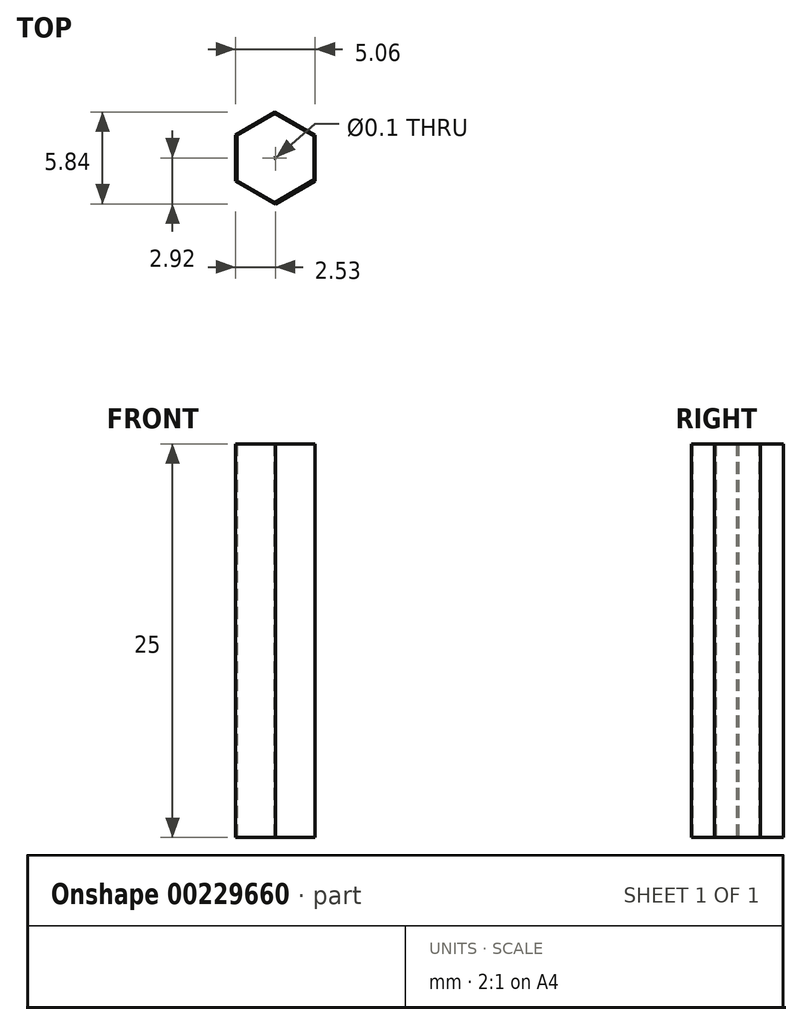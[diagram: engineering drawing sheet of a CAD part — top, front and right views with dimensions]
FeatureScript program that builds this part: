
annotation { "Feature Type Name" : "Feature", "Feature Type Description" : "" }
export const myFeature = defineFeature(function(context is Context, id is Id, definition is map)
    precondition{}
    {
        {
            var Q0;
            Q0=qCreatedBy(makeId("Top.planeOp"),FACE);
            var sketch = newSketch(context, id + "F0", { "sketchPlane" : qUnion([Q0])});
            skLineSegment(sketch, "E0.0", {"start": v(2.53, 1.46) * mm, "end": v(2.53, -1.46) * mm});
            skLineSegment(sketch, "E0.1", {"start": v(2.53, -1.46) * mm, "end": v(0, -2.92) * mm});
            skLineSegment(sketch, "E0.2", {"start": v(0, -2.92) * mm, "end": v(-2.53, -1.46) * mm});
            skLineSegment(sketch, "E0.3", {"start": v(-2.53, -1.46) * mm, "end": v(-2.53, 1.46) * mm});
            skLineSegment(sketch, "E0.4", {"start": v(-2.53, 1.46) * mm, "end": v(0, 2.92) * mm});
            skLineSegment(sketch, "E0.5", {"start": v(0, 2.92) * mm, "end": v(2.53, 1.46) * mm});
            skSolve(sketch);
        }
        {
            var Q0;
            Q0=makeQuery(id+"F0.imprint","IMPRINT",FACE,{"disambiguationData":[TD([[makeQuery(id+"F0.imprint","IMPRINT",EDGE,{"derivedFrom":sQuery(id+"F0.wireOp",EDGE,"E0.0")}),-1.0]])]});
            extrude(context, id + "F1", {"entities" : qUnion([Q0]), "depth" : 25 * mm});
        }
        {
            var Q0;
            Q0=qCreatedBy(makeId("Top.planeOp"),FACE);
            var sketch = newSketch(context, id + "F2", { "sketchPlane" : qUnion([Q0])});
            skLineSegment(sketch, "E1.0", {"start": v(2.5, 1.45) * mm, "end": v(2.5, -1.45) * mm});
            skLineSegment(sketch, "E1.1", {"start": v(2.5, -1.45) * mm, "end": v(0, -2.9) * mm});
            skLineSegment(sketch, "E1.2", {"start": v(0, -2.9) * mm, "end": v(-2.5, -1.45) * mm});
            skLineSegment(sketch, "E1.3", {"start": v(-2.5, -1.45) * mm, "end": v(-2.5, 1.45) * mm});
            skLineSegment(sketch, "E1.4", {"start": v(-2.5, 1.45) * mm, "end": v(0, 2.9) * mm});
            skLineSegment(sketch, "E1.5", {"start": v(0, 2.9) * mm, "end": v(2.5, 1.45) * mm});
            skPoint(sketch, "E1.0.midPoint", {"position": v(2.5, 0) * mm});
            skSolve(sketch);
        }
        {
            var Q0;
            Q0=makeQuery(id+"F2.imprint","IMPRINT",FACE,{"disambiguationData":[TD([[makeQuery(id+"F2.imprint","IMPRINT",EDGE,{"derivedFrom":sQuery(id+"F2.wireOp",EDGE,"E1.0")}),-1.0]])]});
            extrude(context, id + "F3", {"entities" : qUnion([Q0]), "depth" : 25 * mm});
        }
        {
            var Q0;
            Q0=qCreatedBy(makeId("Top.planeOp"),FACE);
            var sketch = newSketch(context, id + "F4", { "sketchPlane" : qUnion([Q0])});
            skCircle(sketch, "E2.cCircle", {"center": v(0, 0) * mm, "radius": 2.47 * mm, "construction": true});
            skLineSegment(sketch, "E2.0", {"start": v(2.47, 1.43) * mm, "end": v(2.47, -1.43) * mm});
            skLineSegment(sketch, "E2.1", {"start": v(2.47, -1.43) * mm, "end": v(0, -2.85) * mm});
            skLineSegment(sketch, "E2.2", {"start": v(0, -2.85) * mm, "end": v(-2.47, -1.43) * mm});
            skLineSegment(sketch, "E2.3", {"start": v(-2.47, -1.43) * mm, "end": v(-2.47, 1.43) * mm});
            skLineSegment(sketch, "E2.4", {"start": v(-2.47, 1.43) * mm, "end": v(0, 2.85) * mm});
            skLineSegment(sketch, "E2.5", {"start": v(0, 2.85) * mm, "end": v(2.47, 1.43) * mm});
            skPoint(sketch, "E2.0.midPoint", {"position": v(2.47, 0) * mm});
            skSolve(sketch);
        }
        {
            var Q0;
            Q0=makeQuery(id+"F4.imprint","IMPRINT",FACE,{"disambiguationData":[TD([[makeQuery(id+"F4.imprint","IMPRINT",EDGE,{"derivedFrom":sQuery(id+"F4.wireOp",EDGE,"E2.0")}),-1.0]])]});
            extrude(context, id + "F5", {"entities" : qUnion([Q0]), "depth" : 25 * mm});
        }
        {
            var Q0;
            Q0=qCreatedBy(makeId("Top.planeOp"),FACE);
            var sketch = newSketch(context, id + "F6", { "sketchPlane" : qUnion([Q0])});
            skCircle(sketch, "E3.cCircle", {"center": v(0, 0) * mm, "radius": 2.5 * mm, "construction": true});
            skLineSegment(sketch, "E3.0", {"start": v(2.5, 1.44) * mm, "end": v(2.5, -1.44) * mm});
            skLineSegment(sketch, "E3.1", {"start": v(2.5, -1.44) * mm, "end": v(0, -2.88) * mm});
            skLineSegment(sketch, "E3.2", {"start": v(0, -2.88) * mm, "end": v(-2.5, -1.44) * mm});
            skLineSegment(sketch, "E3.3", {"start": v(-2.5, -1.44) * mm, "end": v(-2.5, 1.44) * mm});
            skLineSegment(sketch, "E3.4", {"start": v(-2.5, 1.44) * mm, "end": v(0, 2.88) * mm});
            skLineSegment(sketch, "E3.5", {"start": v(0, 2.88) * mm, "end": v(2.5, 1.44) * mm});
            skPoint(sketch, "E3.0.midPoint", {"position": v(2.5, 0) * mm});
            skSolve(sketch);
        }
        {
            var Q0;
            Q0=makeQuery(id+"F6.imprint","IMPRINT",FACE,{"disambiguationData":[TD([[makeQuery(id+"F6.imprint","IMPRINT",EDGE,{"derivedFrom":sQuery(id+"F6.wireOp",EDGE,"E3.0")}),-1.0]])]});
            extrude(context, id + "F7", {"entities" : qUnion([Q0]), "depth" : 25 * mm});
        }
        {
            var Q0;
            Q0=qCreatedBy(makeId("Top.planeOp"),FACE);
            var sketch = newSketch(context, id + "F8", { "sketchPlane" : qUnion([Q0])});
            skLineSegment(sketch, "E4", {"start": v(-0.09, 2.86) * mm, "end": v(2.52, 1.35) * mm});
            skLineSegment(sketch, "E5", {"start": v(2.52, 1.35) * mm, "end": v(2.52, -1.35) * mm});
            skLineSegment(sketch, "E6", {"start": v(2.52, -1.35) * mm, "end": v(-0.09, -2.86) * mm});
            skLineSegment(sketch, "E7", {"start": v(-0.09, -2.86) * mm, "end": v(-2.43, -1.5) * mm});
            skLineSegment(sketch, "E8", {"start": v(-2.43, -1.5) * mm, "end": v(-2.43, 1.5) * mm});
            skLineSegment(sketch, "E9", {"start": v(-2.43, 1.5) * mm, "end": v(-0.09, 2.86) * mm});
            skCircle(sketch, "E10", {"center": v(0, 0) * mm, "radius": 0.05 * mm});
            skPoint(sketch, "E11", {"position": v(0.05, 0) * mm});
            skPoint(sketch, "E12", {"position": v(-0.03, -0.04) * mm});
            skPoint(sketch, "E13", {"position": v(-0.03, 0.04) * mm});
            skSolve(sketch);
        }
        {
            var Q0;
            Q0=makeQuery(id+"F8.imprint","IMPRINT",FACE,{"disambiguationData":[TD([[makeQuery(id+"F8.imprint","IMPRINT",EDGE,{"derivedFrom":sQuery(id+"F8.wireOp",EDGE,"E4")}),-1.0]])]});
            extrude(context, id + "F9", {"entities" : qUnion([Q0]), "depth" : 25 * mm});
        }
    });
